# Revit family: easy_ugr_19_-_microfilm_rl82_0a9c
name_source: partatom
category: Lighting Fixtures
units: mm (PartAtom-declared; Revit-internal decimal feet)

## family parameters
Cut with Voids When Loaded = No
Host = Face
Light Source = No
Part Type = Normal
Room Calculation Point = No
Round Connector Dimension = Use Diameter
Shared = No

## types (1)
- Easy UGR19 - Microfilm (1 x LED, 1300 lm, 3500K)
    Apparent Load = 13 VA
    CIE Flux Codes = 84 99 100 100 89
    Color Rendering = 90
    Color Temperature = 3500K
    Default Elevation = 1800 mm
    Description = RL82 : 
Round fixed luminaire designed to use LED lamps with C.o.B. technology. Version with rim for surface-mounting. Reflector vacuum-metallised with aluminium vapours with an anti-scratch protective layer. Dissipater made of painted grey die-cast aluminium. Product complete with LED lamp in warm white colour tone (3500K) and microfilm that is able to guarantee a light beam of UGR<19 L<3000 cd/m2, which is ideal for environments with video terminals. Luminaire complete with inverter unit for safety light.


RL82.39 - Ø 163 - 3500K - CRI 90 - UGR<19 - INVERTER - White / Aluminium                                 
E80R - Lamp LED 3500K CRI90
    Height = 99 mm
    Lamp = 1 x LED
    Lamp Light Flux = 1300 lm
    Lamp count = 1
    Length = 163 mm
    Lifetime = 100000 h
    Luminous efficacy = 87 lm/W
    Manufacturer = iGuzzini
    ModVariant = No
    Model = RL82
    Mounting Place = Ceiling
    Mounting Type = Surface mounted
    Number of Poles = 1
    OnlyDefault = Yes
    Power Factor = 1
    Product Name = Easy UGR<19 - Microfilm
    Product group = ceiling mounted luminaire
    ProductGroupID = 3
    Protection Class = Protection class
    Protection Degree = Degree of protection
    RLX_Detail_Level = 1
    RLX_Emergency_Light_Flux = 0 lm
    RLX_Emergency_Type = 0
    RLX_Emergency_Type_DB = No
    RlxData = <blob elided: 24181 chars, md5=827810da>
    Socket = socket
    Standby Power = 0 W
    System Light Flux = 1157 lm
    System Power = 13 W
    Type Comments = Product without accessories
    Type Image = easy_ugr_153_img0010384_orig_img0010606_thum.jpg
    URL = http://relux.com
    VarID = ---
    Voltage = 0 V
    Weight = 0.00 kg
    Width = 0 mm  [stored 0 ft]

note: [stored X ft] marks values corroborated as IEEE doubles in the binary element streams (Revit-internal decimal feet)

## geometry (parser evidence)
native form markers: Blend x4, Sweep x17
no freeform markers — native parametric forms only
